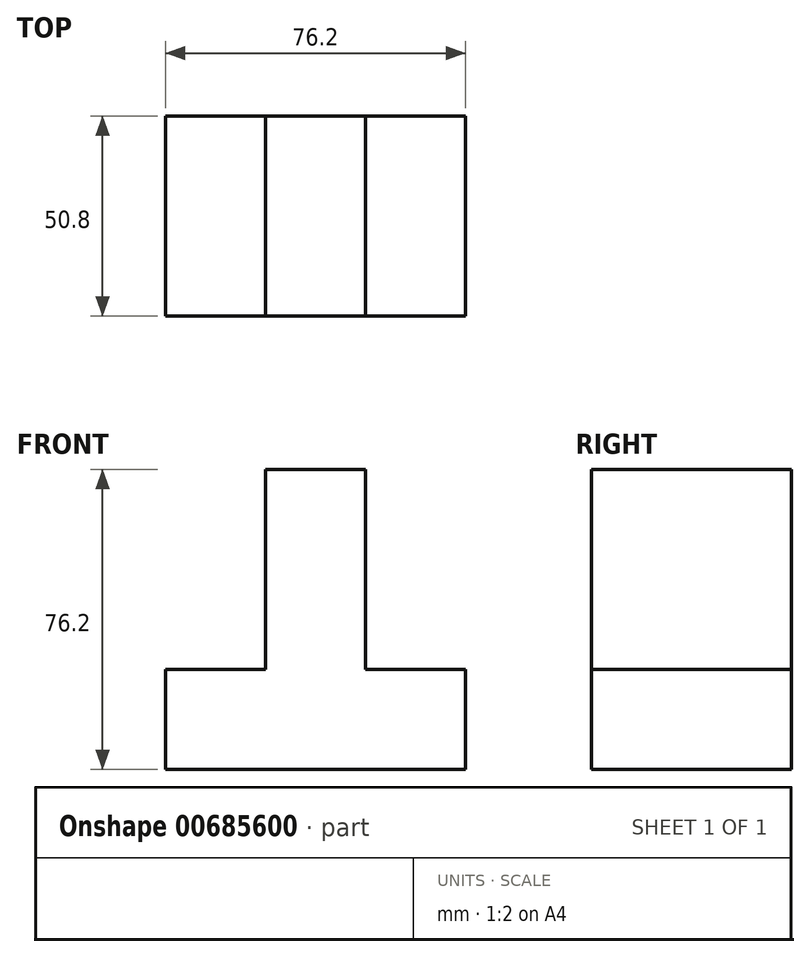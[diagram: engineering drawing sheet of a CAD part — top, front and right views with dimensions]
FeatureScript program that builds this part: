
annotation { "Feature Type Name" : "Feature", "Feature Type Description" : "" }
export const myFeature = defineFeature(function(context is Context, id is Id, definition is map)
    precondition{}
    {
        {
            var Q0;
            Q0=qCreatedBy(makeId("Front.planeOp"),FACE);
            var sketch = newSketch(context, id + "F0", { "sketchPlane" : qUnion([Q0])});
            skLineSegment(sketch, "E0", {"start": v(0, 25.4) * mm, "end": v(0, 0) * mm});
            skLineSegment(sketch, "E1", {"start": v(0, 0) * mm, "end": v(-76.2, 0) * mm});
            skLineSegment(sketch, "E2", {"start": v(-76.2, 0) * mm, "end": v(-76.2, 25.4) * mm});
            skLineSegment(sketch, "E3", {"start": v(-76.2, 25.4) * mm, "end": v(-50.8, 25.4) * mm});
            skLineSegment(sketch, "E4", {"start": v(-50.8, 25.4) * mm, "end": v(-50.8, 76.2) * mm});
            skLineSegment(sketch, "E5", {"start": v(-50.8, 76.2) * mm, "end": v(-25.4, 76.2) * mm});
            skLineSegment(sketch, "E6", {"start": v(-25.4, 76.2) * mm, "end": v(-25.4, 25.4) * mm});
            skLineSegment(sketch, "E7", {"start": v(-25.4, 25.4) * mm, "end": v(0, 25.4) * mm});
            skSolve(sketch);
        }
        {
            var Q0;
            Q0 = qSketchRegion(id + "F0", true);
            extrude(context, id + "F1", {"entities" : qUnion([Q0]), "depth" : 50.8 * mm, "offsetDistance" : 25.4 * mm});
        }
    });
